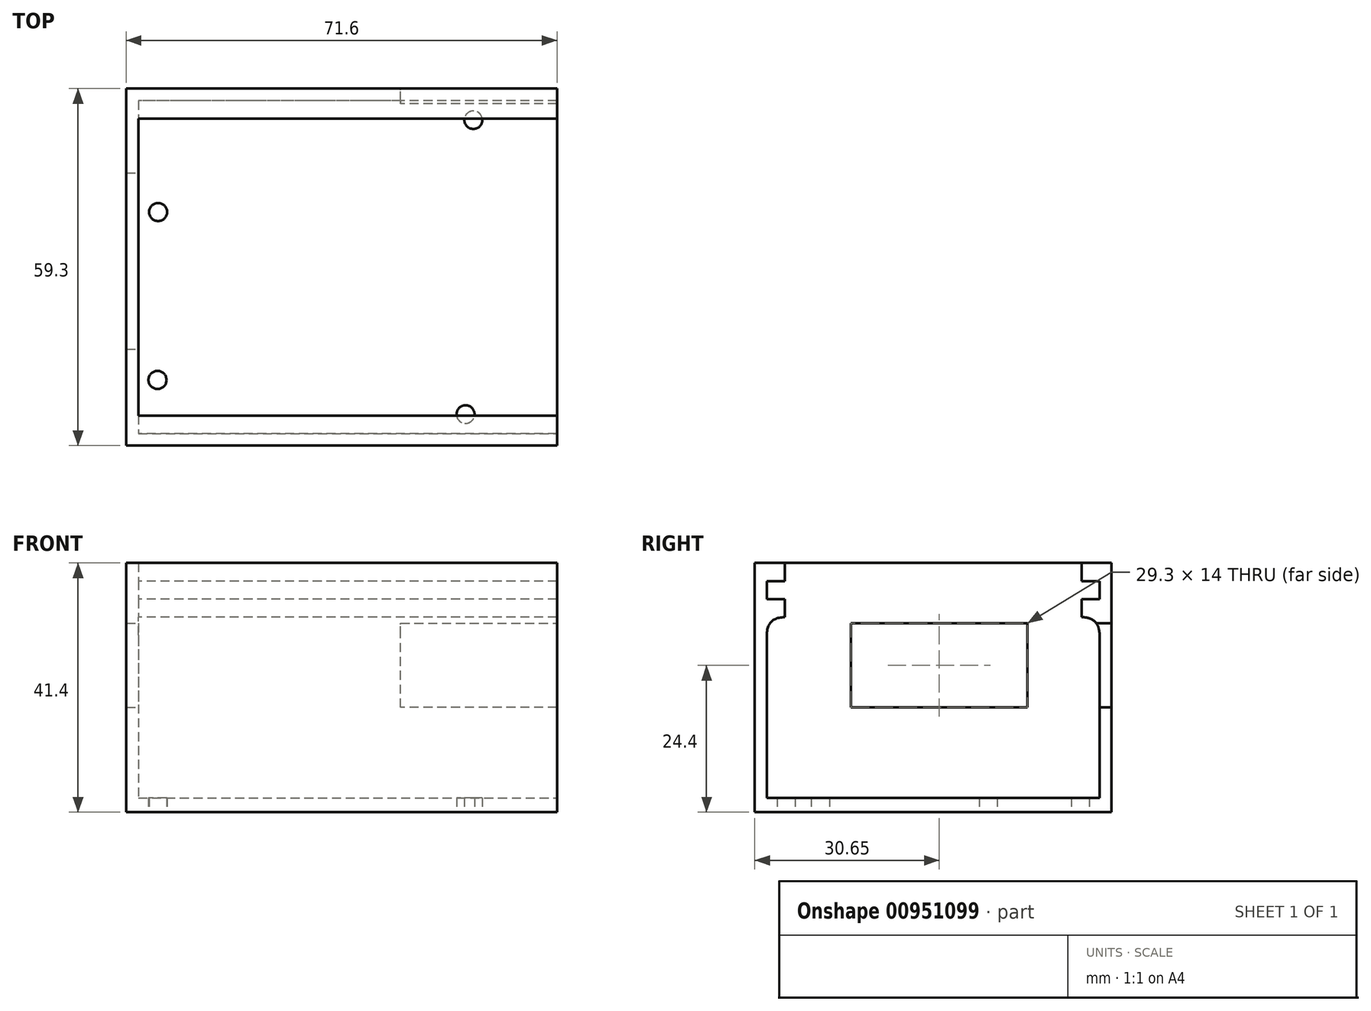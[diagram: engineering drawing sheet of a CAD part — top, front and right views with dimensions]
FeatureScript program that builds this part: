
annotation { "Feature Type Name" : "Feature", "Feature Type Description" : "" }
export const myFeature = defineFeature(function(context is Context, id is Id, definition is map)
    precondition{}
    {
        {
            var Q0;
            Q0=qCreatedBy(makeId("Top.planeOp"),FACE);
            var sketch = newSketch(context, id + "F0", { "sketchPlane" : qUnion([Q0])});
            skLineSegment(sketch, "E0", {"start": v(-68.6, 53.3) * mm, "end": v(-68.6, 0) * mm});
            skLineSegment(sketch, "E1", {"start": v(-68.6, 0) * mm, "end": v(0, 0) * mm});
            skLineSegment(sketch, "E2", {"start": v(-68.6, 53.3) * mm, "end": v(0, 53.3) * mm});
            skLineSegment(sketch, "E3", {"start": v(0, 53.3) * mm, "end": v(0, 0) * mm});
            skCircle(sketch, "E4", {"center": v(-66.4, 7.9) * mm, "radius": 1.5 * mm});
            skCircle(sketch, "E5", {"center": v(-66.3, 35.8) * mm, "radius": 1.5 * mm});
            skCircle(sketch, "E6", {"center": v(-13.9, 51.1) * mm, "radius": 1.5 * mm});
            skCircle(sketch, "E7", {"center": v(-15.2, 2.2) * mm, "radius": 1.5 * mm});
            skSolve(sketch);
        }
        {
            var Q0;
            Q0=qCreatedBy(makeId("Top.planeOp"),FACE);
            var sketch = newSketch(context, id + "F1", { "sketchPlane" : qUnion([Q0])});
            skLineSegment(sketch, "E8.0", {"start": v(-68.6, 53.3) * mm, "end": v(-68.6, 0) * mm});
            skLineSegment(sketch, "E8.1", {"start": v(-68.6, 0) * mm, "end": v(0, 0) * mm});
            skLineSegment(sketch, "E8.2", {"start": v(-68.6, 53.3) * mm, "end": v(0, 53.3) * mm});
            skLineSegment(sketch, "E8.3", {"start": v(0, 53.3) * mm, "end": v(0, 0) * mm});
            skLineSegment(sketch, "E9", {"start": v(-71.6, 56.3) * mm, "end": v(-71.6, -3) * mm});
            skLineSegment(sketch, "E10", {"start": v(-71.6, -3) * mm, "end": v(0, -3) * mm});
            skLineSegment(sketch, "E11", {"start": v(0, -3) * mm, "end": v(0, 56.3) * mm});
            skLineSegment(sketch, "E12", {"start": v(-71.6, 56.3) * mm, "end": v(0, 56.3) * mm});
            skCircle(sketch, "E13.0", {"center": v(-15.2, 2.2) * mm, "radius": 1.5 * mm});
            skCircle(sketch, "E13.1", {"center": v(-13.9, 51.1) * mm, "radius": 1.5 * mm});
            skCircle(sketch, "E13.2", {"center": v(-66.3, 35.8) * mm, "radius": 1.5 * mm});
            skCircle(sketch, "E13.3", {"center": v(-66.4, 7.9) * mm, "radius": 1.5 * mm});
            skSolve(sketch);
        }
        {
            var Q0;
            Q0=makeQuery(id+"F1.imprint","IMPRINT",FACE,{"disambiguationData":[TD([[makeQuery(id+"F1.imprint","IMPRINT",EDGE,{"derivedFrom":sQuery(id+"F1.wireOp",EDGE,"E8.0")}),-1.0]])]});
            var Q1;
            Q1=makeQuery(id+"F1.imprint","IMPRINT",FACE,{"disambiguationData":[TD([[makeQuery(id+"F1.imprint","IMPRINT",EDGE,{"derivedFrom":sQuery(id+"F1.wireOp",EDGE,"E8.0")}),1.0]])]});
            extrude(context, id + "F2", {"entities" : qUnion([Q0, Q1]), "depth" : 2.4 * mm, "offsetDistance" : 25.4 * mm});
        }
        {
            var Q0;
            Q0=makeQuery(id+"F2.opExtrude","CAP_FACE",FACE,{"disambiguationData":[OSD([sQuery(id+"F1.wireOp",EDGE,"E9"),sQuery(id+"F1.wireOp",EDGE,"E10"),sQuery(id+"F1.wireOp",EDGE,"E11"),sQuery(id+"F1.wireOp",EDGE,"E12"),sQuery(id+"F1.wireOp",EDGE,"E13.0"),sQuery(id+"F1.wireOp",EDGE,"E13.1"),sQuery(id+"F1.wireOp",EDGE,"E13.2"),sQuery(id+"F1.wireOp",EDGE,"E13.3")])],"isStart":false});
            var sketch = newSketch(context, id + "F3", { "sketchPlane" : qUnion([Q0])});
            skLineSegment(sketch, "E14", {"start": v(0, 56.3) * mm, "end": v(-71.6, 56.3) * mm});
            skLineSegment(sketch, "E15", {"start": v(-71.6, 56.3) * mm, "end": v(-71.6, -3) * mm});
            skLineSegment(sketch, "E16", {"start": v(-71.6, -3) * mm, "end": v(0, -3) * mm});
            skLineSegment(sketch, "E17", {"start": v(0, -3) * mm, "end": v(0, -1) * mm});
            skLineSegment(sketch, "E18", {"start": v(0, -1) * mm, "end": v(-69.6, -1) * mm});
            skLineSegment(sketch, "E19", {"start": v(-69.6, -1) * mm, "end": v(-69.6, 54.3) * mm});
            skLineSegment(sketch, "E20", {"start": v(-69.6, 54.3) * mm, "end": v(0, 54.3) * mm});
            skLineSegment(sketch, "E21", {"start": v(0, 54.3) * mm, "end": v(0, 56.3) * mm});
            skSolve(sketch);
        }
        {
            var Q0;
            Q0 = qSketchRegion(id + "F3", true);
            extrude(context, id + "F4", {"entities" : qUnion([Q0]), "operationType" : NewBodyOperationType.ADD, "depth" : 39 * mm, "offsetDistance" : 25.4 * mm});
        }
        {
            var Q0;
            Q0=makeQuery(id+"F4.opExtrude","SWEPT_FACE",FACE,{"disambiguationData":[OSD([sQuery(id+"F3.wireOp",EDGE,"E19")])]});
            var sketch = newSketch(context, id + "F5", { "sketchPlane" : qUnion([Q0])});
            skLineSegment(sketch, "E22", {"start": v(-1, 41.4) * mm, "end": v(2, 41.4) * mm});
            skLineSegment(sketch, "E23", {"start": v(2, 41.4) * mm, "end": v(2, 38.4) * mm});
            skLineSegment(sketch, "E24", {"start": v(2, 38.4) * mm, "end": v(-1, 38.4) * mm});
            skLineSegment(sketch, "E25", {"start": v(-1, 38.4) * mm, "end": v(-1, 35.4) * mm});
            skLineSegment(sketch, "E26", {"start": v(-1, 35.4) * mm, "end": v(2, 35.4) * mm});
            skLineSegment(sketch, "E27", {"start": v(2, 35.4) * mm, "end": v(2, 32.4) * mm});
            skLineSegment(sketch, "E28", {"start": v(2, 32.4) * mm, "end": v(-1, 32.4) * mm});
            skLineSegment(sketch, "E29", {"start": v(-1, 32.4) * mm, "end": v(-2.37, 32.4) * mm});
            skLineSegment(sketch, "E30", {"start": v(-2.37, 32.4) * mm, "end": v(-2.37, 41.4) * mm});
            skLineSegment(sketch, "E31", {"start": v(-2.37, 41.4) * mm, "end": v(-1, 41.4) * mm});
            skLineSegment(sketch, "E32", {"start": v(26.65, 2.4) * mm, "end": v(26.65, 41.4) * mm});
            skLineSegment(sketch, "E33.MirrorCS", {"start": v(55.67, 41.4) * mm, "end": v(54.3, 41.4) * mm});
            skLineSegment(sketch, "E34.MirrorCS", {"start": v(54.3, 32.4) * mm, "end": v(55.67, 32.4) * mm});
            skLineSegment(sketch, "E35.MirrorCS", {"start": v(51.3, 35.4) * mm, "end": v(51.3, 32.4) * mm});
            skLineSegment(sketch, "E36.MirrorCS", {"start": v(54.3, 41.4) * mm, "end": v(51.3, 41.4) * mm});
            skLineSegment(sketch, "E37.MirrorCS", {"start": v(51.3, 32.4) * mm, "end": v(54.3, 32.4) * mm});
            skLineSegment(sketch, "E38.MirrorCS", {"start": v(54.3, 35.4) * mm, "end": v(51.3, 35.4) * mm});
            skLineSegment(sketch, "E39.MirrorCS", {"start": v(51.3, 41.4) * mm, "end": v(51.3, 38.4) * mm});
            skLineSegment(sketch, "E40.MirrorCS", {"start": v(54.3, 38.4) * mm, "end": v(54.3, 35.4) * mm});
            skLineSegment(sketch, "E41.MirrorCS", {"start": v(51.3, 38.4) * mm, "end": v(54.3, 38.4) * mm});
            skLineSegment(sketch, "E42.MirrorCS", {"start": v(55.67, 32.4) * mm, "end": v(55.67, 41.4) * mm});
            skSolve(sketch);
        }
        {
            var Q0;
            Q0 = qSketchRegion(id + "F5", true);
            var Q1;
            Q1=makeQuery(id+"F4.boolean.opBoolean","MERGE",FACE,{"derivedFrom":[makeQuery(id+"F2.opExtrude","SWEPT_FACE",FACE,{"disambiguationData":[OSD([sQuery(id+"F1.wireOp",EDGE,"E11")])]}),makeQuery(id+"F4.opExtrude","SWEPT_FACE",FACE,{"disambiguationData":[OSD([sQuery(id+"F3.wireOp",EDGE,"E17")])]}),makeQuery(id+"F4.opExtrude","SWEPT_FACE",FACE,{"disambiguationData":[OSD([sQuery(id+"F3.wireOp",EDGE,"E21")])]})]});
            extrude(context, id + "F6", {"entities" : qUnion([Q0]), "operationType" : NewBodyOperationType.ADD, "endBound" : BoundingType.UP_TO_SURFACE, "depth" : 25.4 * mm, "endBoundEntityFace" : qUnion([Q1]), "offsetDistance" : 25.4 * mm});
        }
        {
            var Q0;
            Q0=makeQuery(id+"F6.boolean.opBoolean","INTERSECT",EDGE,{"derivedFrom":[makeQuery(id+"F4.opExtrude","SWEPT_FACE",FACE,{"disambiguationData":[OSD([sQuery(id+"F3.wireOp",EDGE,"E18")])]}),makeQuery(id+"F6.opExtrude","SWEPT_FACE",FACE,{"disambiguationData":[OSD([sQuery(id+"F5.wireOp",EDGE,"E28"),sQuery(id+"F5.wireOp",EDGE,"E29")])]})]});
            var Q1;
            Q1=makeQuery(id+"F6.boolean.opBoolean","INTERSECT",EDGE,{"derivedFrom":[makeQuery(id+"F4.opExtrude","SWEPT_FACE",FACE,{"disambiguationData":[OSD([sQuery(id+"F3.wireOp",EDGE,"E20")])]}),makeQuery(id+"F6.opExtrude","SWEPT_FACE",FACE,{"disambiguationData":[OSD([sQuery(id+"F5.wireOp",EDGE,"E34.MirrorCS"),sQuery(id+"F5.wireOp",EDGE,"E37.MirrorCS")])]})]});
            fillet(context, id + "F7", {"entities" : qUnion([Q0, Q1]), "radius" : 3 * mm, "tangentPropagation" : true, "rho" : 0.5, "crossSection" : FilletCrossSection.CONIC, "allowEdgeOverflow" : false});
        }
        {
            var Q0;
            Q0=makeQuery(id+"F4.opExtrude","SWEPT_FACE",FACE,{"disambiguationData":[OSD([sQuery(id+"F3.wireOp",EDGE,"E19")])]});
            var sketch = newSketch(context, id + "F8", { "sketchPlane" : qUnion([Q0])});
            skLineSegment(sketch, "E43", {"start": v(13, 31.4) * mm, "end": v(42.3, 31.4) * mm});
            skLineSegment(sketch, "E44", {"start": v(42.3, 31.4) * mm, "end": v(42.3, 17.4) * mm});
            skLineSegment(sketch, "E45", {"start": v(42.3, 17.4) * mm, "end": v(13, 17.4) * mm});
            skLineSegment(sketch, "E46", {"start": v(13, 17.4) * mm, "end": v(13, 31.4) * mm});
            skSolve(sketch);
        }
        {
            var Q0;
            Q0 = qSketchRegion(id + "F8", true);
            var Q1;
            Q1 = qConstructionFilter(qBodyType(qCreatedBy(id + "F8" ,EDGE), BodyType.WIRE), ConstructionObject.NO);
            extrude(context, id + "F9", {"entities" : qUnion([Q0]), "operationType" : NewBodyOperationType.REMOVE, "surfaceEntities" : qUnion([Q1]), "oppositeDirection" : true, "depth" : 25.4 * mm, "offsetDistance" : 25.4 * mm});
        }
        {
            var Q0;
            Q0=makeQuery(id+"F4.boolean.opBoolean","MERGE",FACE,{"derivedFrom":[makeQuery(id+"F2.opExtrude","SWEPT_FACE",FACE,{"disambiguationData":[OSD([sQuery(id+"F1.wireOp",EDGE,"E12")])]}),makeQuery(id+"F4.opExtrude","SWEPT_FACE",FACE,{"disambiguationData":[OSD([sQuery(id+"F3.wireOp",EDGE,"E14")])]})]});
            var sketch = newSketch(context, id + "F10", { "sketchPlane" : qUnion([Q0])});
            skLineSegment(sketch, "E47", {"start": v(0, 17.4) * mm, "end": v(26, 17.4) * mm});
            skLineSegment(sketch, "E48", {"start": v(26, 17.4) * mm, "end": v(26, 31.4) * mm});
            skLineSegment(sketch, "E49", {"start": v(26, 31.4) * mm, "end": v(0, 31.4) * mm});
            skLineSegment(sketch, "E50", {"start": v(0, 31.4) * mm, "end": v(0, 17.4) * mm});
            skSolve(sketch);
        }
        {
            var Q0;
            Q0=makeQuery(id+"F10.imprint","IMPRINT",FACE,{"disambiguationData":[TD([[makeQuery(id+"F10.imprint","IMPRINT",EDGE,{"derivedFrom":sQuery(id+"F10.wireOp",EDGE,"E47")}),1.0]])]});
            extrude(context, id + "F11", {"entities" : qUnion([Q0]), "operationType" : NewBodyOperationType.REMOVE, "oppositeDirection" : true, "depth" : 25.4 * mm, "offsetDistance" : 25.4 * mm});
        }
    });
